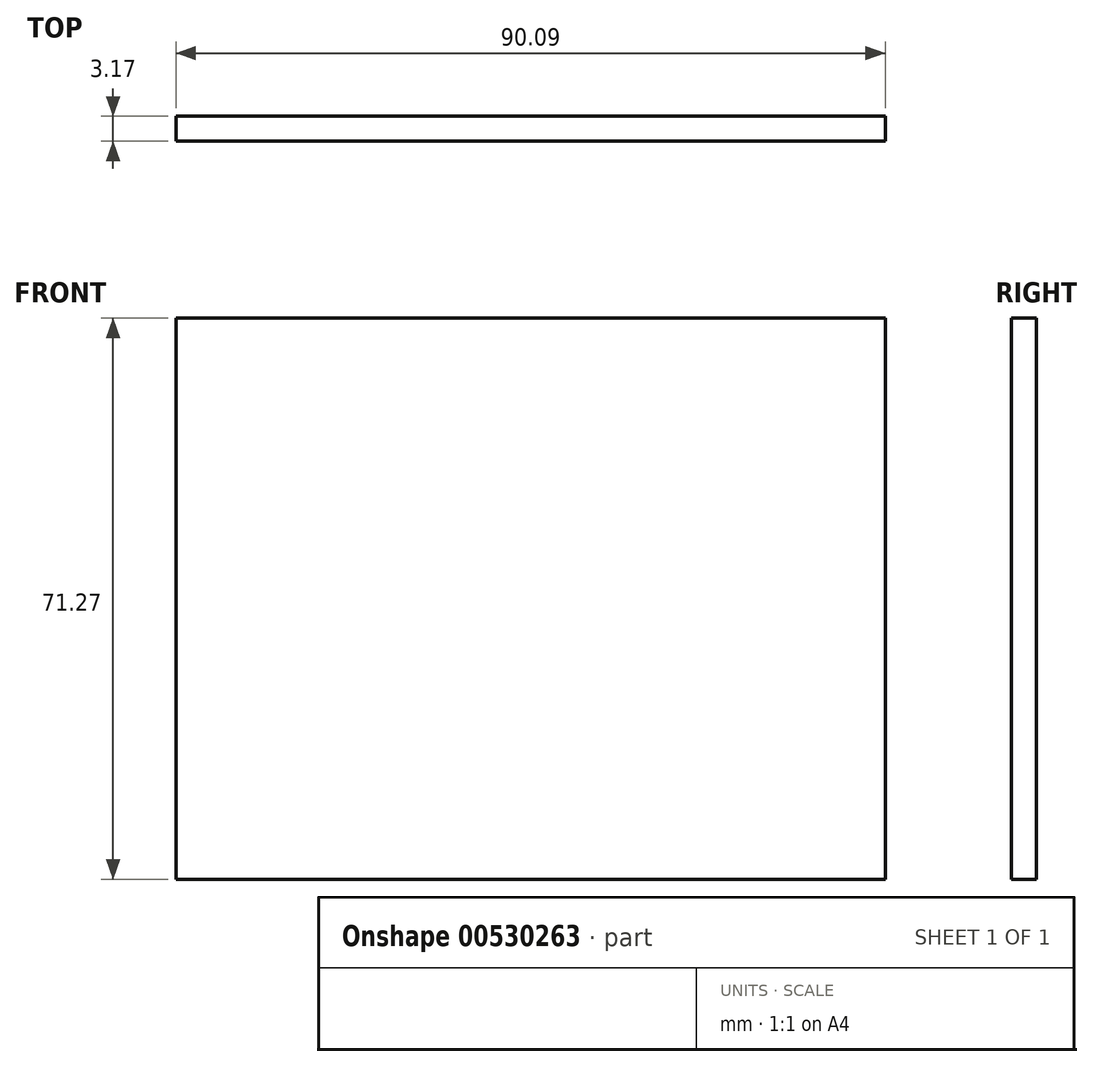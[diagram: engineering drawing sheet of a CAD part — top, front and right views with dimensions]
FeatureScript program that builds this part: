
annotation { "Feature Type Name" : "Feature", "Feature Type Description" : "" }
export const myFeature = defineFeature(function(context is Context, id is Id, definition is map)
    precondition{}
    {
        {
            var Q0;
            Q0=qCreatedBy(makeId("Front.planeOp"),FACE);
            var sketch = newSketch(context, id + "F0", { "sketchPlane" : qUnion([Q0])});
            skLineSegment(sketch, "E0", {"start": v(-49.89, -28.88) * mm, "end": v(40.2, -28.88) * mm});
            skLineSegment(sketch, "E1", {"start": v(40.2, -28.88) * mm, "end": v(40.2, 42.4) * mm});
            skLineSegment(sketch, "E2", {"start": v(40.2, 42.4) * mm, "end": v(-49.89, 42.4) * mm});
            skLineSegment(sketch, "E3", {"start": v(-49.89, 42.4) * mm, "end": v(-49.89, -28.88) * mm});
            skSolve(sketch);
        }
        {
            var Q0;
            Q0=makeQuery(id+"F0.imprint","IMPRINT",FACE,{"disambiguationData":[TD([[makeQuery(id+"F0.imprint","IMPRINT",EDGE,{"derivedFrom":sQuery(id+"F0.wireOp",EDGE,"E0")}),1.0]])]});
            extrude(context, id + "F1", {"entities" : qUnion([Q0]), "depth" : 3.17 * mm, "offsetDistance" : 25.4 * mm});
        }
    });
